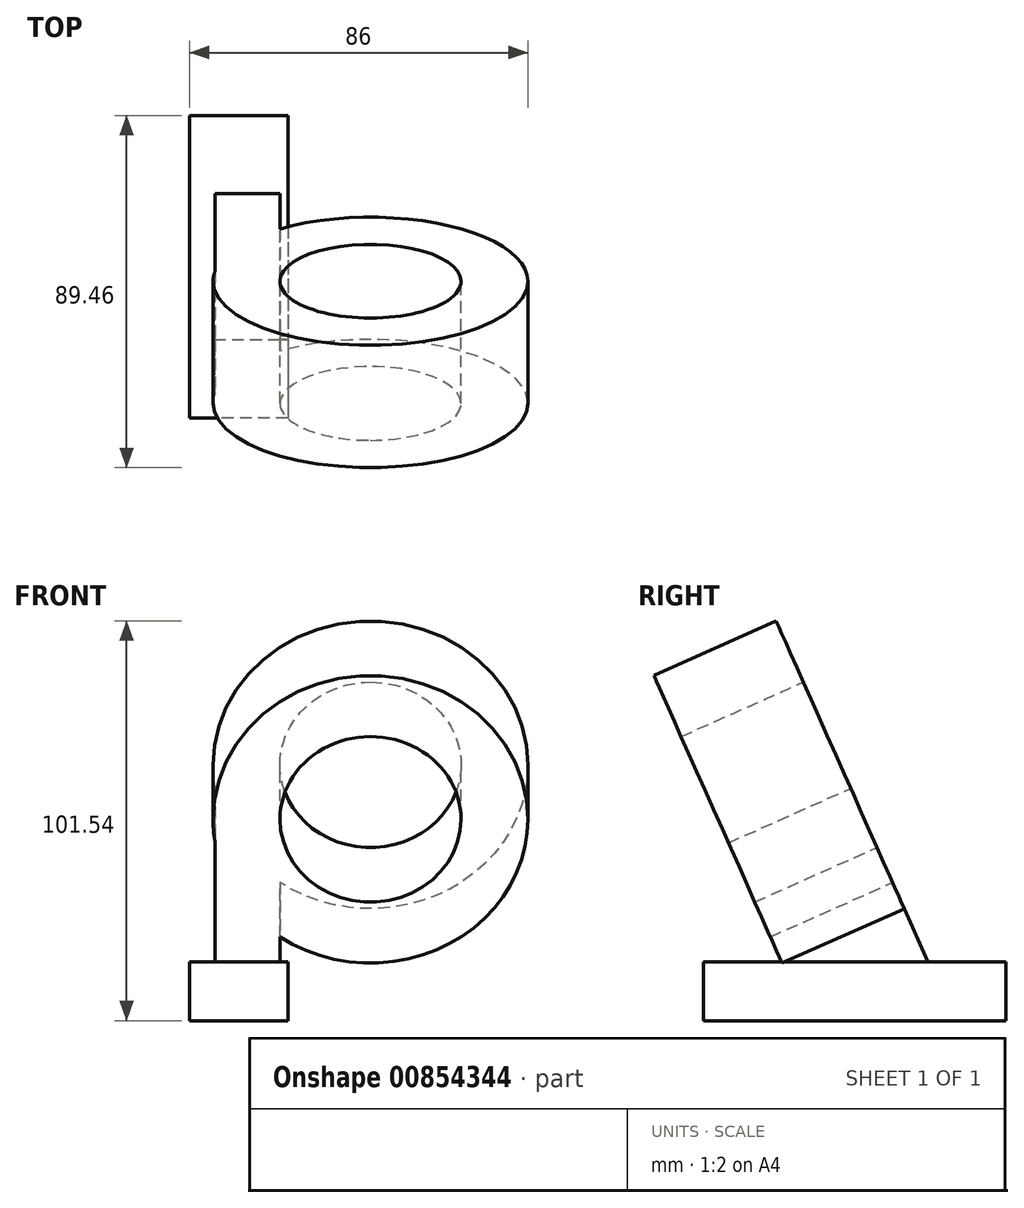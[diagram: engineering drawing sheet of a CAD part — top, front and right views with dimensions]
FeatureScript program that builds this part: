
annotation { "Feature Type Name" : "Feature", "Feature Type Description" : "" }
export const myFeature = defineFeature(function(context is Context, id is Id, definition is map)
    precondition{}
    {
        {
            var Q0;
            Q0=qCreatedBy(makeId("Top.planeOp"),FACE);
            var sketch = newSketch(context, id + "F0", { "sketchPlane" : qUnion([Q0])});
            skLineSegment(sketch, "E0", {"start": v(-39.46, 0) * mm, "end": v(44.1, 0) * mm});
            skSolve(sketch);
        }
        {
            var Q0;
            Q0=sQuery(id+"F0.wireOp",EDGE,"E0");
            cPlane(context, id + "F1", {"entities" : qUnion([Q0]), "cplaneType" : CPlaneType.LINE_ANGLE, "offset" : 25 * mm, "angle" : 24 * degree, "width" : 150 * mm, "height" : 150 * mm});
        }
        {
            var Q0;
            Q0=qCreatedBy(id+"F1.planeOp",FACE);
            var sketch = newSketch(context, id + "F2", { "sketchPlane" : qUnion([Q0])});
            skCircle(sketch, "E1", {"center": v(0, 0) * mm, "radius": 23 * mm});
            skCircle(sketch, "E2", {"center": v(0, 0) * mm, "radius": 40 * mm});
            skSolve(sketch);
        }
        {
            var Q0;
            Q0=qCreatedBy(makeId("Right.planeOp"),FACE);
            var sketch = newSketch(context, id + "F3", { "sketchPlane" : qUnion([Q0])});
            skLineSegment(sketch, "E3.0", {"start": v(-9.35, 21.01) * mm, "end": v(9.35, -21.01) * mm});
            skLineSegment(sketch, "E3.2", {"start": v(-16.27, 36.54) * mm, "end": v(16.27, -36.54) * mm});
            skLineSegment(sketch, "E4", {"start": v(0, 0) * mm, "end": v(0, -65) * mm});
            skLineSegment(sketch, "E5", {"start": v(0, -65) * mm, "end": v(42.13, -65) * mm});
            skLineSegment(sketch, "E6", {"start": v(42.13, -65) * mm, "end": v(-51.88, -65) * mm});
            skSolve(sketch);
        }
        {
            var Q0;
            Q0 = qSketchRegion(id + "F3", true);
            var Q1;
            Q1=makeQuery(id+"F2.imprint","IMPRINT",FACE,{"disambiguationData":[TD([[makeQuery(id+"F2.imprint","IMPRINT",EDGE,{"derivedFrom":sQuery(id+"F2.wireOp",EDGE,"E1")}),-1.0]])]});
            extrude(context, id + "F4", {"entities" : qUnion([Q0, Q1]), "oppositeDirection" : true, "depth" : 34 * mm, "offsetDistance" : 25 * mm});
        }
        {
            var Q0;
            Q0=qCreatedBy(makeId("Right.planeOp"),FACE);
            var sketch = newSketch(context, id + "F5", { "sketchPlane" : qUnion([Q0])});
            skLineSegment(sketch, "E7", {"start": v(16.27, -36.54) * mm, "end": v(-14.8, -50.37) * mm});
            skLineSegment(sketch, "E8", {"start": v(-47.33, 22.71) * mm, "end": v(-16.27, 36.54) * mm});
            skPoint(sketch, "E9.0", {"position": v(-4.87, -65) * mm});
            skLineSegment(sketch, "E10.0", {"start": v(42.13, -65) * mm, "end": v(-51.88, -65) * mm});
            skLineSegment(sketch, "E11", {"start": v(-47.33, 22.71) * mm, "end": v(2.1, -88.3) * mm});
            skLineSegment(sketch, "E12", {"start": v(-16.27, 36.54) * mm, "end": v(32.64, -73.31) * mm});
            skLineSegment(sketch, "E13.0", {"start": v(42.13, -50) * mm, "end": v(-51.88, -50) * mm});
            skLineSegment(sketch, "E14", {"start": v(-14.8, -50.37) * mm, "end": v(-14.8, -72.47) * mm});
            skLineSegment(sketch, "E15", {"start": v(-14.8, -65) * mm, "end": v(-34.8, -65) * mm});
            skLineSegment(sketch, "E16", {"start": v(-34.8, -65) * mm, "end": v(59.64, -65) * mm});
            skLineSegment(sketch, "E17", {"start": v(-14.8, -65) * mm, "end": v(45.2, -65) * mm});
            skLineSegment(sketch, "E18", {"start": v(-34.8, -65) * mm, "end": v(-34.8, -50) * mm});
            skLineSegment(sketch, "E19", {"start": v(42.13, -65) * mm, "end": v(42.13, -50) * mm});
            skSolve(sketch);
        }
        {
            var Q0;
            Q0=qCreatedBy(makeId("Right.planeOp"),FACE);
            cPlane(context, id + "F6", {"entities" : qUnion([Q0]), "cplaneType" : CPlaneType.OFFSET, "offset" : 46 * mm, "oppositeDirection" : true, "width" : 150 * mm, "height" : 150 * mm});
        }
        {
            var Q0;
            Q0=qCreatedBy(id+"F6.planeOp",FACE);
            var sketch = newSketch(context, id + "F7", { "sketchPlane" : qUnion([Q0])});
            skLineSegment(sketch, "E20.0", {"start": v(0, 0) * mm, "end": v(0, -65) * mm});
            skLineSegment(sketch, "E20.1", {"start": v(-34.8, -65) * mm, "end": v(-34.8, -50) * mm});
            skLineSegment(sketch, "E20.2", {"start": v(42.13, -50) * mm, "end": v(-51.88, -50) * mm});
            skLineSegment(sketch, "E20.3", {"start": v(16.27, -36.54) * mm, "end": v(-14.8, -50.37) * mm});
            skLineSegment(sketch, "E20.4", {"start": v(42.13, -65) * mm, "end": v(-51.88, -65) * mm});
            skLineSegment(sketch, "E20.5", {"start": v(-16.27, 36.54) * mm, "end": v(32.64, -73.31) * mm});
            skLineSegment(sketch, "E20.6", {"start": v(-34.8, -65) * mm, "end": v(59.64, -65) * mm});
            skLineSegment(sketch, "E20.7", {"start": v(42.13, -65) * mm, "end": v(42.13, -50) * mm});
            skLineSegment(sketch, "E20.8", {"start": v(-47.33, 22.71) * mm, "end": v(2.1, -88.3) * mm});
            skLineSegment(sketch, "E20.9", {"start": v(-14.8, -50.37) * mm, "end": v(-14.8, -72.47) * mm});
            skLineSegment(sketch, "E20.10", {"start": v(-47.33, 22.71) * mm, "end": v(-14.8, -50.37) * mm});
            skLineSegment(sketch, "E20.11", {"start": v(42.13, -65) * mm, "end": v(-51.88, -65) * mm});
            skLineSegment(sketch, "E21.1", {"start": v(-16.27, 36.54) * mm, "end": v(16.27, -36.54) * mm});
            skLineSegment(sketch, "E21.3", {"start": v(-9.35, 21.01) * mm, "end": v(9.35, -21.01) * mm});
            skLineSegment(sketch, "E21.6", {"start": v(-47.33, 22.71) * mm, "end": v(-16.27, 36.54) * mm});
            skLineSegment(sketch, "E21.14", {"start": v(-9.35, 21.01) * mm, "end": v(9.35, -21.01) * mm});
            skLineSegment(sketch, "E21.15", {"start": v(-16.27, 36.54) * mm, "end": v(16.27, -36.54) * mm});
            skLineSegment(sketch, "E21.18", {"start": v(-16.27, 36.54) * mm, "end": v(16.27, -36.54) * mm});
            skLineSegment(sketch, "E21.19", {"start": v(-9.35, 21.01) * mm, "end": v(9.35, -21.01) * mm});
            skLineSegment(sketch, "E21.20", {"start": v(0, -65) * mm, "end": v(42.13, -65) * mm});
            skSolve(sketch);
        }
        {
            var Q0;
            {var subQ5=sQuery(id+"F7.wireOp",EDGE,"E20.1");Q0=makeQuery(id+"F7.imprint","IMPRINT",FACE,{"disambiguationData":[TD([[makeQuery(id+"F7.imprint","IMPRINT",EDGE,{"derivedFrom":subQ5}),-1.0]])]});}
            var Q1;
            {var subQ0=sQuery(id+"F7.wireOp",EDGE,"E20.7");Q1=makeQuery(id+"F7.imprint","IMPRINT",FACE,{"disambiguationData":[TD([[makeQuery(id+"F7.imprint","IMPRINT",EDGE,{"derivedFrom":subQ0}),1.0]])]});}
            var Q2;
            {var subQ3=sQuery(id+"F7.wireOp",EDGE,"E20.2");var subQ5=sQuery(id+"F7.wireOp",EDGE,"E20.5");var subQ7=makeQuery(id+"F7.imprint","INTERSECT",VERTEX,{"derivedFrom":[subQ3,subQ5]});Q2=makeQuery(id+"F7.imprint","IMPRINT",FACE,{"disambiguationData":[TD([[makeQuery(id+"F7.imprint","IMPRINT",EDGE,{"disambiguationData":[TD([[subQ7,-1.0]])],"derivedFrom":subQ3}),1.0]])]});}
            var Q3;
            {var subQ1=sQuery(id+"F7.wireOp",EDGE,"E20.8");var subQ3=sQuery(id+"F7.wireOp",EDGE,"E20.4");var subQ4=makeQuery(id+"F7.imprint","INTERSECT",VERTEX,{"derivedFrom":[subQ1,subQ3]});Q3=makeQuery(id+"F7.imprint","IMPRINT",FACE,{"disambiguationData":[TD([[makeQuery(id+"F7.imprint","IMPRINT",EDGE,{"disambiguationData":[TD([[subQ4,-1.0]])],"derivedFrom":subQ3}),-1.0]])]});}
            var Q4;
            {var subQ5=sQuery(id+"F7.wireOp",EDGE,"E20.2");var subQ6=sQuery(id+"F7.wireOp",EDGE,"E20.0");var subQ7=makeQuery(id+"F7.imprint","INTERSECT",VERTEX,{"derivedFrom":[subQ6,subQ5]});Q4=makeQuery(id+"F7.imprint","IMPRINT",FACE,{"disambiguationData":[TD([[makeQuery(id+"F7.imprint","IMPRINT",EDGE,{"disambiguationData":[TD([[subQ7,-1.0]])],"derivedFrom":subQ5}),1.0]])]});}
            extrude(context, id + "F8", {"entities" : qUnion([Q0, Q1, Q2, Q3, Q4]), "depth" : 25 * mm, "offsetDistance" : 25 * mm});
        }
        {
            var Q0;
            Q0=qCreatedBy(id+"F1.planeOp",FACE);
            var sketch = newSketch(context, id + "F9", { "sketchPlane" : qUnion([Q0])});
            skLineSegment(sketch, "E22.0", {"start": v(0, 40) * mm, "end": v(0, -40) * mm});
            skLineSegment(sketch, "E22.1", {"start": v(0, 40) * mm, "end": v(0, -80.25) * mm});
            skLineSegment(sketch, "E22.2", {"start": v(0, 40) * mm, "end": v(0, -81.52) * mm});
            skLineSegment(sketch, "E22.3", {"start": v(0, 0) * mm, "end": v(0, -59.38) * mm});
            skLineSegment(sketch, "E22.4", {"start": v(39.46, 0) * mm, "end": v(-44.1, 0) * mm});
            skCircle(sketch, "E22.5", {"center": v(0, 0) * mm, "radius": 23 * mm});
            skCircle(sketch, "E22.6", {"center": v(0, 0) * mm, "radius": 40 * mm});
            skCircle(sketch, "E22.7", {"center": v(0, 0) * mm, "radius": 40 * mm});
            skLineSegment(sketch, "E22.8", {"start": v(0, 40) * mm, "end": v(0, -40) * mm});
            skSolve(sketch);
        }
        {
            var Q0;
            {var subQ3=sQuery(id+"F9.wireOp",EDGE,"E22.5");var subQ6=makeQuery(id+"F9.imprint","INTERSECT",VERTEX,{"disambiguationData":[OD(0.0)],"derivedFrom":[sQuery(id+"F9.wireOp",EDGE,"E22.4"),subQ3]});Q0=makeQuery(id+"F9.imprint","IMPRINT",FACE,{"disambiguationData":[TD([[makeQuery(id+"F9.imprint","IMPRINT",EDGE,{"disambiguationData":[TD([[subQ6,-1.0]])],"derivedFrom":subQ3}),-1.0]])]});}
            var sketch = newSketch(context, id + "F10", { "sketchPlane" : qUnion([Q0])});
            skCircle(sketch, "E23.0", {"center": v(0, 0) * mm, "radius": 23 * mm});
            skLineSegment(sketch, "E23.1", {"start": v(39.46, 0) * mm, "end": v(-44.1, 0) * mm});
            skLineSegment(sketch, "E23.3", {"start": v(0, 40) * mm, "end": v(0, -80.25) * mm});
            skLineSegment(sketch, "E23.4", {"start": v(0, 40) * mm, "end": v(0, -81.52) * mm});
            skLineSegment(sketch, "E23.5", {"start": v(0, 0) * mm, "end": v(0, -59.38) * mm});
            skCircle(sketch, "E23.6", {"center": v(0, 0) * mm, "radius": 40 * mm});
            skCircle(sketch, "E23.8", {"center": v(0, 0) * mm, "radius": 40 * mm});
            skLineSegment(sketch, "E23.9", {"start": v(39.46, 0) * mm, "end": v(-44.1, 0) * mm});
            skLineSegment(sketch, "E23.10", {"start": v(0, 40) * mm, "end": v(0, -80.25) * mm});
            skLineSegment(sketch, "E23.11", {"start": v(0, 40) * mm, "end": v(0, -40) * mm});
            skLineSegment(sketch, "E23.12", {"start": v(0, 0) * mm, "end": v(0, -59.38) * mm});
            skLineSegment(sketch, "E23.13", {"start": v(0, 40) * mm, "end": v(0, -40) * mm});
            skLineSegment(sketch, "E23.14", {"start": v(0, 40) * mm, "end": v(0, -81.52) * mm});
            skLineSegment(sketch, "E24.0", {"start": v(0, -76.52) * mm, "end": v(0, -38.28) * mm});
            skLineSegment(sketch, "E25", {"start": v(39.46, 0) * mm, "end": v(39.46, -86.8) * mm});
            skLineSegment(sketch, "E26", {"start": v(23, 0) * mm, "end": v(23, -89.9) * mm});
            skPoint(sketch, "E27.0.3.start.orphan", {"position": v(21, -76.52) * mm});
            skPoint(sketch, "E28.trimOffspring.end.orphan", {"position": v(21, -62.81) * mm});
            skPoint(sketch, "E27.0.0.end.orphan", {"position": v(46, -62.81) * mm});
            skPoint(sketch, "E29.trimOffspring.end.orphan", {"position": v(46, -76.52) * mm});
            skLineSegment(sketch, "E30", {"start": v(23, -83.89) * mm, "end": v(39.46, -83.89) * mm});
            skSolve(sketch);
        }
        {
            var Q0;
            {var subQ5=sQuery(id+"F10.wireOp",EDGE,"E30");Q0=makeQuery(id+"F10.imprint","IMPRINT",FACE,{"disambiguationData":[TD([[makeQuery(id+"F10.imprint","IMPRINT",EDGE,{"derivedFrom":subQ5}),1.0]])]});}
            var Q1;
            Q1=makeQuery(id+"F4.opExtrude","CAP_FACE",FACE,{"disambiguationData":[OSD([sQuery(id+"F2.wireOp",EDGE,"E1"),sQuery(id+"F2.wireOp",EDGE,"E2")])],"isStart":false});
            extrude(context, id + "F11", {"entities" : qUnion([Q0]), "operationType" : NewBodyOperationType.ADD, "endBound" : BoundingType.UP_TO_SURFACE, "oppositeDirection" : true, "depth" : 25 * mm, "endBoundEntityFace" : qUnion([Q1]), "offsetDistance" : 25 * mm});
        }
        {
            var Q0;
            {var subQ0=sQuery(id+"F10.wireOp",EDGE,"E30");var subQ1=sQuery(id+"F10.wireOp",EDGE,"E25");Q0=makeQuery(id+"F11.boolean.opBoolean","SPLIT",FACE,{"disambiguationData":[TD([makeQuery(id+"F11.opExtrude","SWEPT_FACE",FACE,{"disambiguationData":[OSD([subQ0])]})])],"derivedFrom":makeQuery(id+"F11.opExtrude","SWEPT_FACE",FACE,{"disambiguationData":[OSD([subQ1])]})});}
            extrude(context, id + "F12", {"entities" : qUnion([Q0]), "operationType" : NewBodyOperationType.REMOVE, "oppositeDirection" : true, "depth" : 25 * mm, "offsetDistance" : 25 * mm});
        }
        {
            var Q0;
            {var subQ0=sQuery(id+"F9.wireOp",EDGE,"E22.7");var subQ1=sQuery(id+"F9.wireOp",EDGE,"E22.4");var subQ2=makeQuery(id+"F9.imprint","INTERSECT",VERTEX,{"derivedFrom":[subQ1,subQ0]});Q0=makeQuery(id+"F9.imprint","IMPRINT",FACE,{"disambiguationData":[TD([[makeQuery(id+"F9.imprint","IMPRINT",EDGE,{"disambiguationData":[TD([[subQ2,1.0]])],"derivedFrom":subQ1}),-1.0]])]});}
            extrude(context, id + "F13", {"entities" : qUnion([Q0]), "operationType" : NewBodyOperationType.REMOVE, "oppositeDirection" : true, "depth" : 180.6 * mm, "offsetDistance" : 25 * mm});
        }
        {
            var Q0;
            {var subQ0=sQuery(id+"F2.wireOp",EDGE,"E2");var subQ7=sQuery(id+"F10.wireOp",EDGE,"E25");Q0=makeQuery(id+"F11.boolean.opBoolean","SPLIT",FACE,{"disambiguationData":[TD([makeQuery(id+"F4.opExtrude","SWEPT_FACE",FACE,{"disambiguationData":[OSD([subQ0])]})])],"derivedFrom":makeQuery(id+"F11.opExtrude","SWEPT_FACE",FACE,{"disambiguationData":[OSD([subQ7])]})});}
            var sketch = newSketch(context, id + "F14", { "sketchPlane" : qUnion([Q0])});
            skLineSegment(sketch, "E31", {"start": v(14.96, -50) * mm, "end": v(13.96, -50) * mm});
            skSolve(sketch);
        }
        {
            var Q0;
            Q0=makeQuery(id+"F14.imprint","IMPRINT",FACE,{"disambiguationData":[TD([[makeQuery(id+"F14.imprint","IMPRINT",EDGE,{"derivedFrom":sQuery(id+"F14.wireOp",EDGE,"E31")}),1.0]])]});
            extrude(context, id + "F15", {"entities" : qUnion([Q0]), "operationType" : NewBodyOperationType.ADD, "depth" : 6.54 * mm, "offsetDistance" : 25 * mm});
        }
    });
